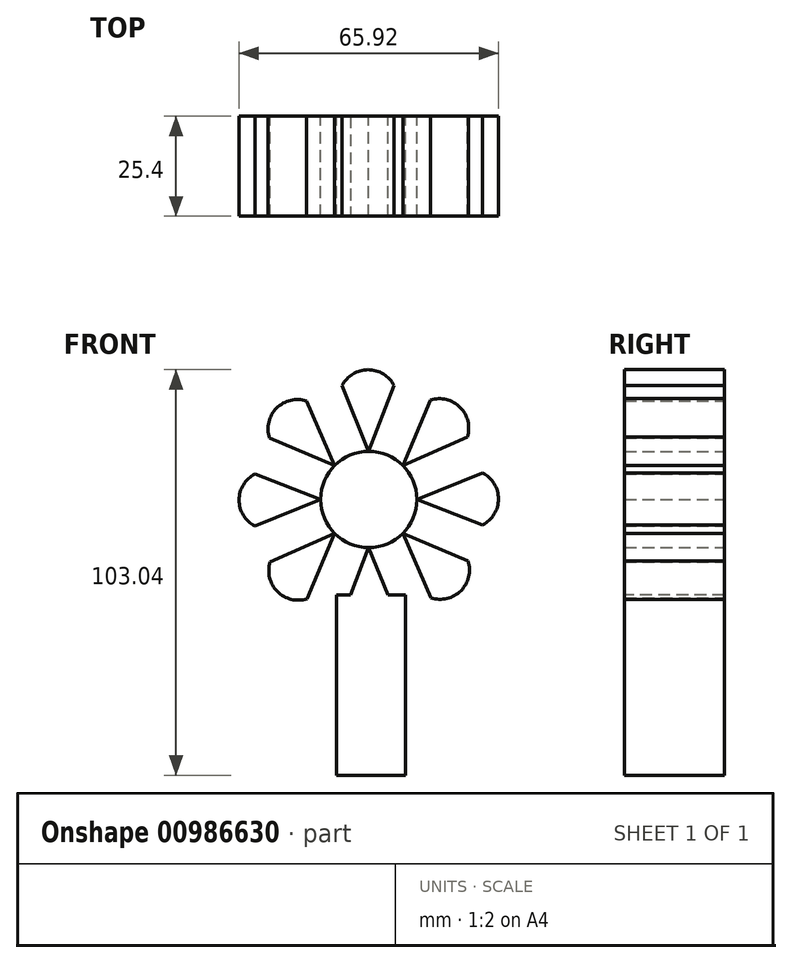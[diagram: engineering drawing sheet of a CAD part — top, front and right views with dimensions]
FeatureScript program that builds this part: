
annotation { "Feature Type Name" : "Feature", "Feature Type Description" : "" }
export const myFeature = defineFeature(function(context is Context, id is Id, definition is map)
    precondition{}
    {
        {
            var Q0;
            Q0=qCreatedBy(makeId("Front.planeOp"),FACE);
            var sketch = newSketch(context, id + "F0", { "sketchPlane" : qUnion([Q0])});
            skLineSegment(sketch, "E0.bottom", {"start": v(-8.2, -70.08) * mm, "end": v(9.35, -70.08) * mm});
            skLineSegment(sketch, "E0.top", {"start": v(-8.2, -24.32) * mm, "end": v(9.35, -24.32) * mm});
            skLineSegment(sketch, "E0.left", {"start": v(-8.2, -70.08) * mm, "end": v(-8.2, -24.32) * mm});
            skLineSegment(sketch, "E0.right", {"start": v(9.35, -70.08) * mm, "end": v(9.35, -24.32) * mm});
            skSolve(sketch);
        }
        {
            var Q0;
            Q0 = qSketchRegion(id + "F0", true);
            extrude(context, id + "F1", {"entities" : qUnion([Q0]), "depth" : 25.4 * mm, "offsetDistance" : 25.4 * mm});
        }
        {
            var Q0;
            Q0=qCreatedBy(makeId("Front.planeOp"),FACE);
            var sketch = newSketch(context, id + "F2", { "sketchPlane" : qUnion([Q0])});
            skCircle(sketch, "E1", {"center": v(0, 0) * mm, "radius": 12.23 * mm});
            skLineSegment(sketch, "E2", {"start": v(12.23, 0) * mm, "end": v(28.92, 6.76) * mm});
            skArc(sketch, "E3", {"start": v(28.92, -6.48) * mm, "mid": v(32.96, 0.14) * mm, "end": v(28.92, 6.76) * mm});
            skLineSegment(sketch, "E4", {"start": v(28.92, -6.48) * mm, "end": v(12.23, 0) * mm});
            skLineSegment(sketch, "E5.1.0", {"start": v(25.03, 15.87) * mm, "end": v(8.64, 8.64) * mm});
            skArc(sketch, "E5.1.1", {"start": v(25.03, 15.87) * mm, "mid": v(23.2, 23.4) * mm, "end": v(15.67, 25.24) * mm});
            skLineSegment(sketch, "E5.1.2", {"start": v(8.64, 8.64) * mm, "end": v(15.67, 25.24) * mm});
            skLineSegment(sketch, "E5.2.0", {"start": v(6.48, 28.92) * mm, "end": v(0, 12.23) * mm});
            skArc(sketch, "E5.2.1", {"start": v(6.48, 28.92) * mm, "mid": v(-0.14, 32.96) * mm, "end": v(-6.76, 28.92) * mm});
            skLineSegment(sketch, "E5.2.2", {"start": v(0, 12.23) * mm, "end": v(-6.76, 28.92) * mm});
            skLineSegment(sketch, "E5.3.0", {"start": v(-15.87, 25.03) * mm, "end": v(-8.64, 8.64) * mm});
            skArc(sketch, "E5.3.1", {"start": v(-15.87, 25.03) * mm, "mid": v(-23.4, 23.2) * mm, "end": v(-25.24, 15.67) * mm});
            skLineSegment(sketch, "E5.3.2", {"start": v(-8.64, 8.64) * mm, "end": v(-25.24, 15.67) * mm});
            skLineSegment(sketch, "E5.4.0", {"start": v(-28.92, 6.48) * mm, "end": v(-12.23, 0) * mm});
            skArc(sketch, "E5.4.1", {"start": v(-28.92, 6.48) * mm, "mid": v(-32.96, -0.14) * mm, "end": v(-28.92, -6.76) * mm});
            skLineSegment(sketch, "E5.4.2", {"start": v(-12.23, 0) * mm, "end": v(-28.92, -6.76) * mm});
            skLineSegment(sketch, "E5.5.0", {"start": v(-25.03, -15.87) * mm, "end": v(-8.64, -8.64) * mm});
            skArc(sketch, "E5.5.1", {"start": v(-25.03, -15.87) * mm, "mid": v(-23.2, -23.4) * mm, "end": v(-15.67, -25.24) * mm});
            skLineSegment(sketch, "E5.5.2", {"start": v(-8.64, -8.64) * mm, "end": v(-15.67, -25.24) * mm});
            skLineSegment(sketch, "E5.6.0", {"start": v(-6.48, -28.92) * mm, "end": v(0, -12.23) * mm});
            skArc(sketch, "E5.6.1", {"start": v(-6.48, -28.92) * mm, "mid": v(0.14, -32.96) * mm, "end": v(6.76, -28.92) * mm});
            skLineSegment(sketch, "E5.6.2", {"start": v(0, -12.23) * mm, "end": v(6.76, -28.92) * mm});
            skLineSegment(sketch, "E5.7.0", {"start": v(15.87, -25.03) * mm, "end": v(8.64, -8.64) * mm});
            skArc(sketch, "E5.7.1", {"start": v(15.87, -25.03) * mm, "mid": v(23.4, -23.2) * mm, "end": v(25.24, -15.67) * mm});
            skLineSegment(sketch, "E5.7.2", {"start": v(8.64, -8.64) * mm, "end": v(25.24, -15.67) * mm});
            skSolve(sketch);
        }
        {
            var Q0;
            Q0=makeQuery(id+"F2.imprint","IMPRINT",FACE,{"disambiguationData":[TD([[makeQuery(id+"F2.imprint","IMPRINT",EDGE,{"derivedFrom":sQuery(id+"F2.wireOp",EDGE,"E5.7.0")}),-1.0]])]});
            var Q1;
            Q1=makeQuery(id+"F2.imprint","IMPRINT",FACE,{"disambiguationData":[TD([[makeQuery(id+"F2.imprint","IMPRINT",EDGE,{"derivedFrom":sQuery(id+"F2.wireOp",EDGE,"E2")}),-1.0]])]});
            extrude(context, id + "F3", {"entities" : qUnion([Q0, Q1]), "depth" : 25.4 * mm, "offsetDistance" : 25.4 * mm});
        }
        {
            var Q0;
            Q0=makeQuery(id+"F2.imprint","IMPRINT",FACE,{"disambiguationData":[TD([[makeQuery(id+"F2.imprint","IMPRINT",EDGE,{"derivedFrom":sQuery(id+"F2.wireOp",EDGE,"E5.1.0")}),-1.0]])]});
            extrude(context, id + "F4", {"entities" : qUnion([Q0]), "depth" : 25.4 * mm, "offsetDistance" : 25.4 * mm});
        }
        {
            var Q0;
            Q0=makeQuery(id+"F2.imprint","IMPRINT",FACE,{"disambiguationData":[TD([[makeQuery(id+"F2.imprint","IMPRINT",EDGE,{"derivedFrom":sQuery(id+"F2.wireOp",EDGE,"E5.3.0")}),-1.0]])]});
            extrude(context, id + "F5", {"entities" : qUnion([Q0]), "depth" : 25.4 * mm, "offsetDistance" : 25.4 * mm});
        }
        {
            var Q0;
            Q0=makeQuery(id+"F2.imprint","IMPRINT",FACE,{"disambiguationData":[TD([[makeQuery(id+"F2.imprint","IMPRINT",EDGE,{"derivedFrom":sQuery(id+"F2.wireOp",EDGE,"E5.4.0")}),-1.0]])]});
            extrude(context, id + "F6", {"entities" : qUnion([Q0]), "depth" : 25.4 * mm, "offsetDistance" : 25.4 * mm});
        }
        {
            var Q0;
            Q0=makeQuery(id+"F2.imprint","IMPRINT",FACE,{"disambiguationData":[TD([[makeQuery(id+"F2.imprint","IMPRINT",EDGE,{"derivedFrom":sQuery(id+"F2.wireOp",EDGE,"E5.2.0")}),-1.0]])]});
            extrude(context, id + "F7", {"entities" : qUnion([Q0]), "depth" : 25.4 * mm, "offsetDistance" : 25.4 * mm});
        }
        {
            var Q0;
            Q0=makeQuery(id+"F2.imprint","IMPRINT",FACE,{"disambiguationData":[TD([[makeQuery(id+"F2.imprint","IMPRINT",EDGE,{"derivedFrom":sQuery(id+"F2.wireOp",EDGE,"E5.5.0")}),-1.0]])]});
            extrude(context, id + "F8", {"entities" : qUnion([Q0]), "depth" : 25.4 * mm, "offsetDistance" : 25.4 * mm});
        }
        {
            var Q0;
            Q0=makeQuery(id+"F2.imprint","IMPRINT",FACE,{"disambiguationData":[TD([[makeQuery(id+"F2.imprint","IMPRINT",EDGE,{"derivedFrom":sQuery(id+"F2.wireOp",EDGE,"E5.6.0")}),-1.0]])]});
            extrude(context, id + "F9", {"entities" : qUnion([Q0]), "operationType" : NewBodyOperationType.ADD, "depth" : 25.4 * mm, "offsetDistance" : 25.4 * mm});
        }
        {
            var Q0;
            {var subQ0=sQuery(id+"F2.wireOp",EDGE,"E1");var subQ5=makeQuery(id+"F2.imprint","INTERSECT",VERTEX,{"derivedFrom":[subQ0,sQuery(id+"F2.wireOp",EDGE,"E2"),sQuery(id+"F2.wireOp",EDGE,"E4")]});Q0=makeQuery(id+"F2.imprint","IMPRINT",FACE,{"disambiguationData":[TD([[makeQuery(id+"F2.imprint","IMPRINT",EDGE,{"disambiguationData":[TD([[subQ5,-1.0]])],"derivedFrom":subQ0}),1.0]])]});}
            extrude(context, id + "F10", {"entities" : qUnion([Q0]), "depth" : 25.4 * mm, "offsetDistance" : 25.4 * mm});
        }
    });
